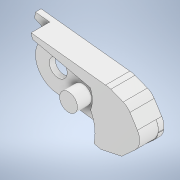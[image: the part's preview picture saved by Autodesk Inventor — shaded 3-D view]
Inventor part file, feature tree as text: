
AUTODESK INVENTOR PART (.ipt)
format: ipt  version: 2022 (Build 260153000, 153)  size: 188,928 bytes
history: native  units: in
note: dims shown in document units (in); Inventor stores cm internally (conversion verified against a paired STEP export)
features: extrude x3, sketch x2, other x1
ambient origin geometry x8: Origin, YZ Plane, XZ Plane, XY Plane, X Axis, Y Axis, Z Axis, Center Point
bodies: Body1 (feature_tree)
feature tree (6):
  other  "Sólido1"
  extrude  "Extrusión1"  Depth=0.252in
  extrude  "Extrusión5"  Depth=0.0787in
  extrude  "Extrusión6"  Depth=0.0787in
  sketch  "Boceto5"  dims[d0=0.0984in d4=0.252in]
  sketch  "Boceto6"  dims[d5=0.1634in d6=0.4055in d7=0.1496in d8=0.0709in d9=0.4331in d10=0.2756in d11=0.0315in d12=0.0in d19=0.0787in d24=0.1024in d25=0.0in d26=0.0984in d27=0.0787in d28=0.0in]
